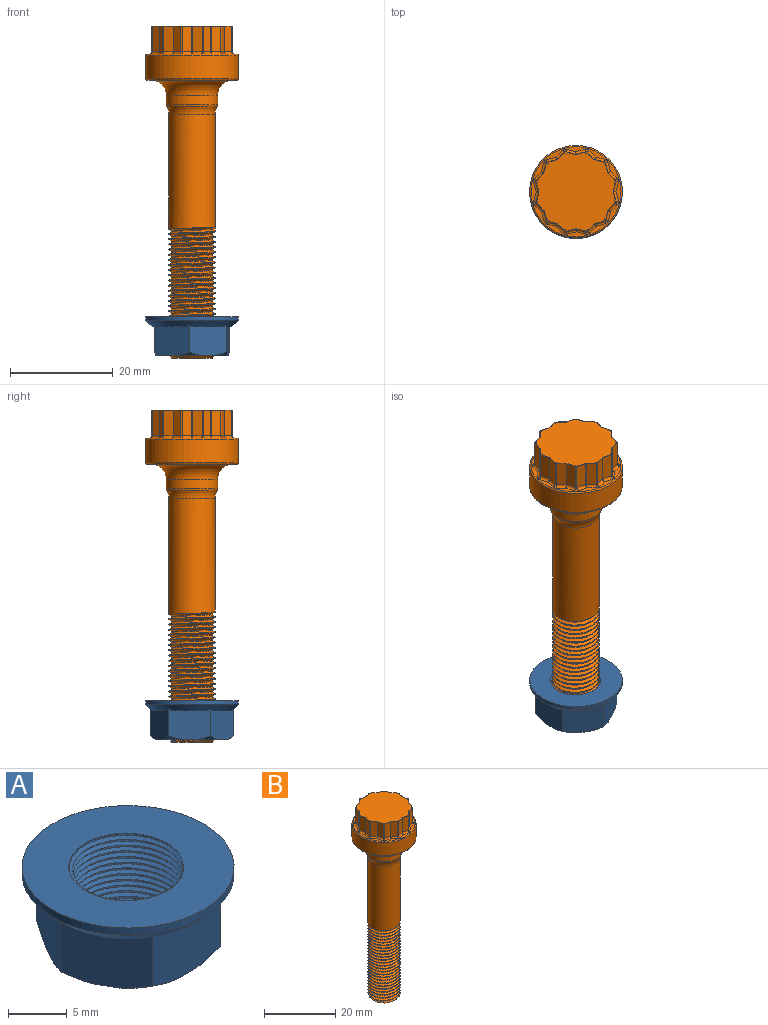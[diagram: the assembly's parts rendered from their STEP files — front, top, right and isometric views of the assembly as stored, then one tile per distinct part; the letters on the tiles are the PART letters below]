
ASSEMBLY  parts=2 mates=1
PART A: 29 faces, bbox 18.3x18.3x8.2 mm
  f0: plane 14.22x14mm, normal (0,0,-1), area 79.2mm2, adj f1,f2,f3,f4,f5,f6,f17,f18
  f1: plane 7.34x6.28mm, normal (-0.87,0.5,0), area 43.7mm2, adj f0,f2,f6,f7,f16,f18,f22
  f2: plane 7.34x6.28mm, normal (-0.87,-0.5,0), area 43.7mm2, adj f0,f1,f3,f15,f16,f21,f22
  f3: plane 8.43x6.28mm, normal (0,-1,0), area 43.7mm2, adj f0,f2,f4,f11,f16,f20,f21
  f4: plane 7.34x6.28mm, normal (0.87,-0.5,0), area 43.7mm2, adj f0,f3,f5,f10,f16,f19,f20
  f5: plane 7.34x6.28mm, normal (0.87,0.5,0), area 43.7mm2, adj f0,f4,f6,f9,f16,f17,f19
  f6: plane 8.43x6.28mm, normal (0,1,0), area 43.7mm2, adj f0,f1,f5,f8,f16,f17,f18
  f7: plane 5.76x3.33mm, normal (0,0,-1), area 3.4mm2, adj f1,f16
  f8: plane 6.65x0.75mm, normal (0,0,-1), area 3.4mm2, adj f6,f16
  f9: plane 5.76x3.33mm, normal (0,0,-1), area 3.4mm2, adj f5,f16
  f10: plane 5.76x3.33mm, normal (0,0,-1), area 3.4mm2, adj f4,f16
  f11: plane 6.65x0.75mm, normal (0,0,-1), area 3.4mm2, adj f3,f16
  f12: cylinder r=9mm len=18mm, axis (0,0,1), area 42.4mm2, adj f13,f16
  f13: plane 18.2x18.2mm, normal (0,0,1), area 178.6mm2, adj f12,f25,f27,f28
  f14: cylinder r=4.5mm len=9mm, axis (0,0,-1), area 7.1mm2, adj f23,f24,f26
  f15: plane 5.76x3.33mm, normal (0,0,-1), area 3.4mm2, adj f2,f16
  f16: cone r=9mm half-angle=45deg, axis (0,0,1), area 91.2mm2, adj f1,f2,f3,f4,f5,f6,f7,f8
  f17: cone r=8.83mm half-angle=52deg, axis (0,0,1), area 3.2mm2, adj f0,f5,f6
  f18: cone r=8.83mm half-angle=52deg, axis (0,0,1), area 3.2mm2, adj f0,f1,f6
  f19: cone r=8.83mm half-angle=52deg, axis (0,0,1), area 3.2mm2, adj f0,f4,f5
  f20: cone r=8.83mm half-angle=52deg, axis (0,0,1), area 3.2mm2, adj f0,f3,f4
  f21: cone r=8.83mm half-angle=52deg, axis (0,0,1), area 3.2mm2, adj f0,f2,f3
  f22: cone r=8.83mm half-angle=52deg, axis (0,0,1), area 3.2mm2, adj f0,f1,f2
  f23: cone r=4.5mm half-angle=45deg, axis (0,0,-1), area 21.1mm2, adj f0,f14,f24,f26
  f24: plane 0.68x0.53mm, normal (0,1,0), area 0.2mm2, adj f14,f23,f25,f26,f27,f28
  f25: bspline ~11.57x10.02mm, area 126.1mm2, adj f13,f24,f27,f28
  f26: bspline ~10.82x9.37mm, area 6.1mm2, adj f14,f23,f24,f27
  f27: bspline ~11.57x10.02mm, area 133.8mm2, adj f13,f24,f25,f26,f28
  f28: bspline ~11.64x10.08mm, area 80.9mm2, adj f13,f24,f25,f27
PART B: 201 faces, bbox 19.5x19.5x64.9 mm
  f0: cylinder r=4.5mm len=22.84mm, axis (0,0,1), area 631.6mm2, adj f25,f192,f194,f195
  f1: cylinder r=4.5mm len=3.35mm, axis (0,0,1), area 0.3mm2, adj f2,f27,f196,f197
  f2: cylinder r=4.5mm len=9mm, axis (0,0,1), area 3.7mm2, adj f1,f3,f195,f197
  f3: cylinder r=4.5mm len=9mm, axis (0,0,1), area 3.7mm2, adj f2,f4,f195,f197
  f4: cylinder r=4.5mm len=9mm, axis (0,0,1), area 3.7mm2, adj f3,f5,f195,f197
  f5: cylinder r=4.5mm len=9mm, axis (0,0,1), area 3.8mm2, adj f4,f6,f195,f197
  f6: cylinder r=4.5mm len=9mm, axis (0,0,1), area 3.7mm2, adj f5,f7,f195,f197
  f7: cylinder r=4.5mm len=9mm, axis (0,0,1), area 3.7mm2, adj f6,f8,f195,f197
  f8: cylinder r=4.5mm len=9mm, axis (0,0,1), area 3.7mm2, adj f7,f9,f195,f197
  f9: cylinder r=4.5mm len=9mm, axis (0,0,1), area 3.8mm2, adj f8,f10,f195,f197
  f10: cylinder r=4.5mm len=9mm, axis (0,0,1), area 3.7mm2, adj f9,f11,f195,f197
  f11: cylinder r=4.5mm len=9mm, axis (0,0,1), area 3.7mm2, adj f10,f12,f195,f197
  f12: cylinder r=4.5mm len=9mm, axis (0,0,1), area 3.7mm2, adj f11,f13,f195,f197
  f13: cylinder r=4.5mm len=9mm, axis (0,0,1), area 3.8mm2, adj f12,f14,f195,f197
  f14: cylinder r=4.5mm len=9mm, axis (0,0,1), area 3.7mm2, adj f13,f15,f195,f197
  f15: cylinder r=4.5mm len=9mm, axis (0,0,1), area 3.7mm2, adj f14,f16,f195,f197
  f16: cylinder r=4.5mm len=9mm, axis (0,0,1), area 3.7mm2, adj f15,f17,f195,f197
  f17: cylinder r=4.5mm len=9mm, axis (0,0,1), area 3.8mm2, adj f16,f18,f195,f197
  f18: cylinder r=4.5mm len=9mm, axis (0,0,1), area 3.7mm2, adj f17,f19,f195,f197
  f19: cylinder r=4.5mm len=9mm, axis (0,0,1), area 3.7mm2, adj f18,f20,f195,f197
  f20: cylinder r=4.5mm len=9mm, axis (0,0,1), area 3.7mm2, adj f19,f21,f195,f197
  f21: cylinder r=4.5mm len=9mm, axis (0,0,1), area 3.8mm2, adj f20,f22,f195,f197
  f22: cylinder r=4.5mm len=9mm, axis (0,0,1), area 3.7mm2, adj f21,f23,f195,f197
  f23: cylinder r=4.5mm len=9mm, axis (0,0,1), area 3.7mm2, adj f22,f24,f195,f197
  f24: cylinder r=4.5mm len=9mm, axis (0,0,1), area 3.7mm2, adj f23,f25,f195,f197
  f25: cylinder r=4.5mm len=9mm, axis (0,0,1), area 3.7mm2, adj f0,f24,f195,f197
  f26: plane 8.02x8.02mm, normal (0,0,-1), area 50.2mm2, adj f27,f196,f198,f200
  f27: cone r=4mm half-angle=45deg, axis (0,0,1), area 9.8mm2, adj f1,f26,f196,f197,f200
  f28: plane 15.15x15.15mm, normal (0,0,1), area 176.8mm2, adj f142,f143,f144,f145,f146,f147,f148,f149
  f29: plane 4.94x1.38mm, normal (0.71,0.71,0), area 9.6mm2, adj f64,f65,f80,f141,f186
  f30: plane 4.94x1.89mm, normal (-0.26,0.97,0), area 9.6mm2, adj f53,f65,f84,f141,f182
  f31: plane 4.94x1.89mm, normal (0.26,0.97,0), area 9.6mm2, adj f53,f66,f88,f140,f178
  f32: plane 4.94x1.38mm, normal (-0.71,0.71,0), area 9.6mm2, adj f54,f66,f92,f140,f174
  f33: plane 4.94x1.89mm, normal (-0.26,0.97,0), area 9.6mm2, adj f54,f67,f96,f139,f170
  f34: plane 4.94x1.89mm, normal (-0.97,0.26,0), area 9.6mm2, adj f55,f67,f100,f139,f166
  f35: plane 4.94x1.38mm, normal (-0.71,0.71,0), area 9.6mm2, adj f55,f68,f104,f138,f162
  f36: plane 4.94x1.89mm, normal (-0.97,-0.26,0), area 9.6mm2, adj f56,f68,f108,f138,f158
  f37: plane 4.94x1.89mm, normal (-0.97,0.26,0), area 9.6mm2, adj f56,f69,f112,f137,f154
  f38: plane 4.94x1.38mm, normal (-0.71,-0.71,0), area 9.6mm2, adj f57,f69,f116,f137,f150
  f39: plane 4.94x1.89mm, normal (-0.97,-0.26,0), area 9.6mm2, adj f57,f70,f120,f136,f146
  f40: plane 4.94x1.89mm, normal (-0.26,-0.97,0), area 9.6mm2, adj f58,f70,f124,f136,f142
  f41: plane 4.94x1.38mm, normal (-0.71,-0.71,0), area 9.6mm2, adj f58,f71,f127,f135,f144
  f42: plane 4.94x1.89mm, normal (0.26,-0.97,0), area 9.6mm2, adj f59,f71,f123,f135,f148
  f43: plane 4.94x1.89mm, normal (-0.26,-0.97,0), area 9.6mm2, adj f59,f72,f119,f134,f152
  f44: plane 4.94x1.38mm, normal (0.71,-0.71,0), area 9.6mm2, adj f60,f72,f115,f134,f156
  f45: plane 4.94x1.89mm, normal (0.26,-0.97,0), area 9.6mm2, adj f60,f73,f111,f133,f160
  f46: plane 4.94x1.89mm, normal (0.97,-0.26,0), area 9.6mm2, adj f61,f73,f107,f133,f164
  f47: plane 4.94x1.38mm, normal (0.71,-0.71,0), area 9.6mm2, adj f61,f74,f103,f132,f168
  f48: plane 4.94x1.89mm, normal (0.97,0.26,0), area 9.6mm2, adj f62,f74,f99,f132,f172
  f49: plane 4.94x1.89mm, normal (0.97,-0.26,0), area 9.6mm2, adj f62,f75,f95,f131,f176
  f50: plane 4.94x1.38mm, normal (0.71,0.71,0), area 9.6mm2, adj f63,f75,f91,f131,f180
  f51: plane 4.94x1.89mm, normal (0.97,0.26,0), area 9.6mm2, adj f63,f76,f87,f130,f184
  f52: plane 4.94x1.89mm, normal (0.26,0.97,0), area 9.6mm2, adj f64,f76,f83,f130,f188
  f53: cylinder r=0.25mm len=4.94mm, axis (0,0,-1), area 0.6mm2, adj f30,f31,f86,f181
  f54: cylinder r=0.25mm len=4.94mm, axis (0,0,1), area 0.6mm2, adj f32,f33,f94,f173
  f55: cylinder r=0.25mm len=4.94mm, axis (0,0,-1), area 0.6mm2, adj f34,f35,f102,f165
  f56: cylinder r=0.25mm len=4.94mm, axis (0,0,-1), area 0.6mm2, adj f36,f37,f110,f157
  f57: cylinder r=0.25mm len=4.94mm, axis (0,0,1), area 0.6mm2, adj f38,f39,f118,f149
  f58: cylinder r=0.25mm len=4.94mm, axis (0,0,-1), area 0.6mm2, adj f40,f41,f126,f143
  f59: cylinder r=0.25mm len=4.94mm, axis (0,0,1), area 0.6mm2, adj f42,f43,f121,f151
  f60: cylinder r=0.25mm len=4.94mm, axis (0,0,-1), area 0.6mm2, adj f44,f45,f113,f159
  f61: cylinder r=0.25mm len=4.94mm, axis (0,0,1), area 0.6mm2, adj f46,f47,f105,f167
  f62: cylinder r=0.25mm len=4.94mm, axis (0,0,1), area 0.6mm2, adj f48,f49,f97,f175
  f63: cylinder r=0.25mm len=4.94mm, axis (0,0,-1), area 0.6mm2, adj f50,f51,f89,f183
  f64: cylinder r=0.25mm len=4.94mm, axis (0,0,-1), area 0.6mm2, adj f29,f52,f81,f189
  f65: cylinder r=0.25mm len=4.92mm, axis (0,0,-1), area 1.3mm2, adj f29,f30,f82,f141
  f66: cylinder r=0.25mm len=4.92mm, axis (0,0,1), area 1.3mm2, adj f31,f32,f90,f140
  f67: cylinder r=0.25mm len=4.92mm, axis (0,0,1), area 1.3mm2, adj f33,f34,f98,f139
  f68: cylinder r=0.25mm len=4.92mm, axis (0,0,1), area 1.3mm2, adj f35,f36,f106,f138
  f69: cylinder r=0.25mm len=4.92mm, axis (0,0,1), area 1.3mm2, adj f37,f38,f114,f137
  f70: cylinder r=0.25mm len=4.92mm, axis (0,0,-1), area 1.3mm2, adj f39,f40,f122,f136
  f71: cylinder r=0.25mm len=4.92mm, axis (0,0,1), area 1.3mm2, adj f41,f42,f125,f135
  f72: cylinder r=0.25mm len=4.92mm, axis (0,0,-1), area 1.3mm2, adj f43,f44,f117,f134
  f73: cylinder r=0.25mm len=4.92mm, axis (0,0,1), area 1.3mm2, adj f45,f46,f109,f133
  f74: cylinder r=0.25mm len=4.92mm, axis (0,0,1), area 1.3mm2, adj f47,f48,f101,f132
  f75: cylinder r=0.25mm len=4.92mm, axis (0,0,1), area 1.3mm2, adj f49,f50,f93,f131
  f76: cylinder r=0.25mm len=4.92mm, axis (0,0,1), area 1.3mm2, adj f51,f52,f85,f130
  f77: cylinder r=9mm len=18mm, axis (0,0,1), area 254.5mm2, adj f128,f129
  f78: plane 17.5x17.5mm, normal (0,0,-1), area 39.5mm2, adj f129,f191
  f79: plane 17.5x17.5mm, normal (0,0,1), area 32mm2, adj f80,f82,f83,f84,f85,f87,f88,f90
  f80: cylinder r=0.5mm len=1.74mm, axis (-0.71,0.71,0), area 1.5mm2, adj f29,f79,f81,f82
  f81: bspline ~0.57x0.47mm, area 0mm2, adj f64,f80,f83
  f82: torus R=0.75mm, axis (0,0,1), area 0.4mm2, adj f65,f79,f80,f84
  f83: cylinder r=0.5mm len=2.02mm, axis (-0.97,0.26,0), area 1.5mm2, adj f52,f79,f81,f85
  f84: cylinder r=0.5mm len=2.02mm, axis (-0.97,-0.26,0), area 1.5mm2, adj f30,f79,f82,f86
  f85: torus R=0.75mm, axis (0,0,1), area 0.4mm2, adj f76,f79,f83,f87
  f86: bspline ~0.57x0.52mm, area 0mm2, adj f53,f84,f88
  f87: cylinder r=0.5mm len=2.02mm, axis (-0.26,0.97,0), area 1.5mm2, adj f51,f79,f85,f89
  f88: cylinder r=0.5mm len=2.02mm, axis (-0.97,0.26,0), area 1.5mm2, adj f31,f79,f86,f90
  f89: bspline ~0.57x0.47mm, area 0mm2, adj f63,f87,f91
  f90: torus R=0.75mm, axis (0,0,1), area 0.4mm2, adj f66,f79,f88,f92
  f91: cylinder r=0.5mm len=1.74mm, axis (-0.71,0.71,0), area 1.5mm2, adj f50,f79,f89,f93
  f92: cylinder r=0.5mm len=1.74mm, axis (-0.71,-0.71,0), area 1.5mm2, adj f32,f79,f90,f94
  f93: torus R=0.75mm, axis (0,0,1), area 0.4mm2, adj f75,f79,f91,f95
  f94: bspline ~0.57x0.47mm, area 0mm2, adj f54,f92,f96
  f95: cylinder r=0.5mm len=2.02mm, axis (0.26,0.97,0), area 1.5mm2, adj f49,f79,f93,f97
  f96: cylinder r=0.5mm len=2.02mm, axis (-0.97,-0.26,0), area 1.5mm2, adj f33,f79,f94,f98
  f97: bspline ~0.57x0.52mm, area 0mm2, adj f62,f95,f99
  f98: torus R=0.75mm, axis (0,0,1), area 0.4mm2, adj f67,f79,f96,f100
  f99: cylinder r=0.5mm len=2.02mm, axis (-0.26,0.97,0), area 1.5mm2, adj f48,f79,f97,f101
  f100: cylinder r=0.5mm len=2.02mm, axis (-0.26,-0.97,0), area 1.5mm2, adj f34,f79,f98,f102
  f101: torus R=0.75mm, axis (0,0,1), area 0.4mm2, adj f74,f79,f99,f103
  f102: bspline ~0.57x0.47mm, area 0mm2, adj f55,f100,f104
  f103: cylinder r=0.5mm len=1.74mm, axis (0.71,0.71,0), area 1.5mm2, adj f47,f79,f101,f105
  f104: cylinder r=0.5mm len=1.74mm, axis (-0.71,-0.71,0), area 1.5mm2, adj f35,f79,f102,f106
  f105: bspline ~0.57x0.47mm, area 0mm2, adj f61,f103,f107
  f106: torus R=0.75mm, axis (0,0,1), area 0.4mm2, adj f68,f79,f104,f108
  f107: cylinder r=0.5mm len=2.02mm, axis (0.26,0.97,0), area 1.5mm2, adj f46,f79,f105,f109
  f108: cylinder r=0.5mm len=2.02mm, axis (0.26,-0.97,0), area 1.5mm2, adj f36,f79,f106,f110
  f109: torus R=0.75mm, axis (0,0,1), area 0.4mm2, adj f73,f79,f107,f111
  f110: bspline ~0.57x0.52mm, area 0mm2, adj f56,f108,f112
  f111: cylinder r=0.5mm len=2.02mm, axis (0.97,0.26,0), area 1.5mm2, adj f45,f79,f109,f113
  f112: cylinder r=0.5mm len=2.02mm, axis (-0.26,-0.97,0), area 1.5mm2, adj f37,f79,f110,f114
  f113: bspline ~0.57x0.47mm, area 0mm2, adj f60,f111,f115
  f114: torus R=0.75mm, axis (0,0,1), area 0.4mm2, adj f69,f79,f112,f116
  f115: cylinder r=0.5mm len=1.74mm, axis (0.71,0.71,0), area 1.5mm2, adj f44,f79,f113,f117
  f116: cylinder r=0.5mm len=1.74mm, axis (0.71,-0.71,0), area 1.5mm2, adj f38,f79,f114,f118
  f117: torus R=0.75mm, axis (0,0,1), area 0.4mm2, adj f72,f79,f115,f119
  f118: bspline ~0.57x0.47mm, area 0mm2, adj f57,f116,f120
  f119: cylinder r=0.5mm len=2.02mm, axis (0.97,-0.26,0), area 1.5mm2, adj f43,f79,f117,f121
  f120: cylinder r=0.5mm len=2.02mm, axis (0.26,-0.97,0), area 1.5mm2, adj f39,f79,f118,f122
  f121: bspline ~0.57x0.52mm, area 0mm2, adj f59,f119,f123
  f122: torus R=0.75mm, axis (0,0,1), area 0.4mm2, adj f70,f79,f120,f124
  f123: cylinder r=0.5mm len=2.02mm, axis (0.97,0.26,0), area 1.5mm2, adj f42,f79,f121,f125
  f124: cylinder r=0.5mm len=2.02mm, axis (0.97,-0.26,0), area 1.5mm2, adj f40,f79,f122,f126
  f125: torus R=0.75mm, axis (0,0,1), area 0.4mm2, adj f71,f79,f123,f127
  f126: bspline ~0.57x0.47mm, area 0mm2, adj f58,f124,f127
  f127: cylinder r=0.5mm len=1.74mm, axis (0.71,-0.71,0), area 1.5mm2, adj f41,f79,f125,f126
  f128: torus R=8.75mm, axis (0,0,1), area 22mm2, adj f77,f79
  f129: torus R=8.75mm, axis (0,0,1), area 22mm2, adj f77,f78
  f130: cone r=8.16mm half-angle=75deg, axis (0,0,-1), area 0.2mm2, adj f51,f52,f76,f184,f187,f188
  f131: cone r=8.16mm half-angle=75deg, axis (0,0,-1), area 0.2mm2, adj f49,f50,f75,f176,f179,f180
  f132: cone r=8.16mm half-angle=75deg, axis (0,0,-1), area 0.2mm2, adj f47,f48,f74,f168,f171,f172
  f133: cone r=8.16mm half-angle=75deg, axis (0,0,-1), area 0.2mm2, adj f45,f46,f73,f160,f163,f164
  f134: cone r=8.16mm half-angle=75deg, axis (0,0,-1), area 0.2mm2, adj f43,f44,f72,f152,f155,f156
  f135: cone r=8.16mm half-angle=75deg, axis (0,0,-1), area 0.2mm2, adj f41,f42,f71,f144,f147,f148
  f136: cone r=8.16mm half-angle=75deg, axis (0,0,-1), area 0.2mm2, adj f39,f40,f70,f142,f145,f146
  f137: cone r=8.16mm half-angle=75deg, axis (0,0,-1), area 0.2mm2, adj f37,f38,f69,f150,f153,f154
  f138: cone r=8.16mm half-angle=75deg, axis (0,0,-1), area 0.2mm2, adj f35,f36,f68,f158,f161,f162
  f139: cone r=8.16mm half-angle=75deg, axis (0,0,-1), area 0.2mm2, adj f33,f34,f67,f166,f169,f170
  f140: cone r=8.16mm half-angle=75deg, axis (0,0,-1), area 0.2mm2, adj f31,f32,f66,f174,f177,f178
  f141: cone r=8.16mm half-angle=75deg, axis (0,0,-1), area 0.2mm2, adj f29,f30,f65,f182,f185,f186
  f142: cylinder r=0.06mm len=1.8mm, axis (-0.97,0.26,0), area 0.2mm2, adj f28,f40,f136,f143,f145
  f143: torus R=0.31mm, axis (0,0,1), area 0mm2, adj f28,f58,f142,f144
  f144: cylinder r=0.06mm len=1.35mm, axis (-0.71,0.71,0), area 0.2mm2, adj f28,f41,f135,f143,f147
  f145: torus R=7.72mm, axis (0,0,1), area 0mm2, adj f28,f136,f142,f146
  f146: cylinder r=0.06mm len=1.8mm, axis (-0.26,0.97,0), area 0.2mm2, adj f28,f39,f136,f145,f149
  f147: torus R=7.72mm, axis (0,0,1), area 0mm2, adj f28,f135,f144,f148
  f148: cylinder r=0.06mm len=1.8mm, axis (-0.97,-0.26,0), area 0.2mm2, adj f28,f42,f135,f147,f151
  f149: torus R=0.31mm, axis (0,0,1), area 0mm2, adj f28,f57,f146,f150
  f150: cylinder r=0.06mm len=1.35mm, axis (-0.71,0.71,0), area 0.2mm2, adj f28,f38,f137,f149,f153
  f151: torus R=0.31mm, axis (0,0,1), area 0mm2, adj f28,f59,f148,f152
  f152: cylinder r=0.06mm len=1.8mm, axis (-0.97,0.26,0), area 0.2mm2, adj f28,f43,f134,f151,f155
  f153: torus R=7.72mm, axis (0,0,1), area 0mm2, adj f28,f137,f150,f154
  f154: cylinder r=0.06mm len=1.8mm, axis (0.26,0.97,0), area 0.2mm2, adj f28,f37,f137,f153,f157
  f155: torus R=7.72mm, axis (0,0,1), area 0mm2, adj f28,f134,f152,f156
  f156: cylinder r=0.06mm len=1.35mm, axis (-0.71,-0.71,0), area 0.2mm2, adj f28,f44,f134,f155,f159
  f157: torus R=0.31mm, axis (0,0,1), area 0mm2, adj f28,f56,f154,f158
  f158: cylinder r=0.06mm len=1.8mm, axis (-0.26,0.97,0), area 0.2mm2, adj f28,f36,f138,f157,f161
  f159: torus R=0.31mm, axis (0,0,1), area 0mm2, adj f28,f60,f156,f160
  f160: cylinder r=0.06mm len=1.8mm, axis (-0.97,-0.26,0), area 0.2mm2, adj f28,f45,f133,f159,f163
  f161: torus R=7.72mm, axis (0,0,1), area 0mm2, adj f28,f138,f158,f162
  f162: cylinder r=0.06mm len=1.35mm, axis (0.71,0.71,0), area 0.2mm2, adj f28,f35,f138,f161,f165
  f163: torus R=7.72mm, axis (0,0,1), area 0mm2, adj f28,f133,f160,f164
  f164: cylinder r=0.06mm len=1.8mm, axis (-0.26,-0.97,0), area 0.2mm2, adj f28,f46,f133,f163,f167
  f165: torus R=0.31mm, axis (0,0,1), area 0mm2, adj f28,f55,f162,f166
  f166: cylinder r=0.06mm len=1.8mm, axis (0.26,0.97,0), area 0.2mm2, adj f28,f34,f139,f165,f169
  f167: torus R=0.31mm, axis (0,0,1), area 0mm2, adj f28,f61,f164,f168
  f168: cylinder r=0.06mm len=1.35mm, axis (-0.71,-0.71,0), area 0.2mm2, adj f28,f47,f132,f167,f171
  f169: torus R=7.72mm, axis (0,0,1), area 0mm2, adj f28,f139,f166,f170
  f170: cylinder r=0.06mm len=1.8mm, axis (0.97,0.26,0), area 0.2mm2, adj f28,f33,f139,f169,f173
  f171: torus R=7.72mm, axis (0,0,1), area 0mm2, adj f28,f132,f168,f172
  f172: cylinder r=0.06mm len=1.8mm, axis (0.26,-0.97,0), area 0.2mm2, adj f28,f48,f132,f171,f175
  f173: torus R=0.31mm, axis (0,0,1), area 0mm2, adj f28,f54,f170,f174
  f174: cylinder r=0.06mm len=1.35mm, axis (0.71,0.71,0), area 0.2mm2, adj f28,f32,f140,f173,f177
  f175: torus R=0.31mm, axis (0,0,1), area 0mm2, adj f28,f62,f172,f176
  f176: cylinder r=0.06mm len=1.8mm, axis (-0.26,-0.97,0), area 0.2mm2, adj f28,f49,f131,f175,f179
  f177: torus R=7.72mm, axis (0,0,1), area 0mm2, adj f28,f140,f174,f178
  f178: cylinder r=0.06mm len=1.8mm, axis (0.97,-0.26,0), area 0.2mm2, adj f28,f31,f140,f177,f181
  f179: torus R=7.72mm, axis (0,0,1), area 0mm2, adj f28,f131,f176,f180
  f180: cylinder r=0.06mm len=1.35mm, axis (0.71,-0.71,0), area 0.2mm2, adj f28,f50,f131,f179,f183
  f181: torus R=0.31mm, axis (0,0,1), area 0mm2, adj f28,f53,f178,f182
  f182: cylinder r=0.06mm len=1.8mm, axis (0.97,0.26,0), area 0.2mm2, adj f28,f30,f141,f181,f185
  f183: torus R=0.31mm, axis (0,0,1), area 0mm2, adj f28,f63,f180,f184
  f184: cylinder r=0.06mm len=1.8mm, axis (0.26,-0.97,0), area 0.2mm2, adj f28,f51,f130,f183,f187
  f185: torus R=7.72mm, axis (0,0,1), area 0mm2, adj f28,f141,f182,f186
  f186: cylinder r=0.06mm len=1.35mm, axis (0.71,-0.71,0), area 0.2mm2, adj f28,f29,f141,f185,f189
  f187: torus R=7.72mm, axis (0,0,1), area 0mm2, adj f28,f130,f184,f188
  f188: cylinder r=0.06mm len=1.8mm, axis (0.97,-0.26,0), area 0.2mm2, adj f28,f52,f130,f187,f189
  f189: torus R=0.31mm, axis (0,0,1), area 0mm2, adj f28,f64,f186,f188
  f190: cylinder r=5mm len=10mm, axis (0,0,1), area 54.1mm2, adj f191,f193
  f191: torus R=8mm, axis (0,0,1), area 180.3mm2, adj f78,f190
  f192: torus R=7.5mm, axis (0,0,1), area 44.1mm2, adj f0,f193
  f193: torus R=4mm, axis (0,0,1), area 15.7mm2, adj f190,f192
  f194: plane 0.87x0.61mm, normal (0,-1,0), area 0.3mm2, adj f0,f197,f198,f199,f200
  f195: bspline ~25x10.56mm, area 0mm2, adj f0,f2,f3,f4,f5,f6,f7,f8
  f196: plane 0.61x0.51mm, normal (0,1,0), area 0.1mm2, adj f1,f26,f27,f198,f199
  f197: bspline ~24.17x10.55mm, area 4mm2, adj f1,f2,f3,f4,f5,f6,f7,f8
  f198: bspline ~25.23x9.14mm, area 157.2mm2, adj f26,f194,f196,f199,f200
  f199: bspline ~25.32x9mm, area 417.1mm2, adj f194,f195,f196,f198
  f200: bspline ~25.32x10.38mm, area 413.4mm2, adj f26,f27,f194,f197,f198
PLACE A rot(axis=(0,0,1),26.3deg) t=(-11.39,12.36,-15.59)mm
PLACE B rot(axis=(0,0,1),0.3deg) t=(-11.39,12.36,-14.65)mm
MATE cylindrical A.f12 <-> B.f0  axis (0,0,1) through (-11.39,12.36,-65.59)mm
